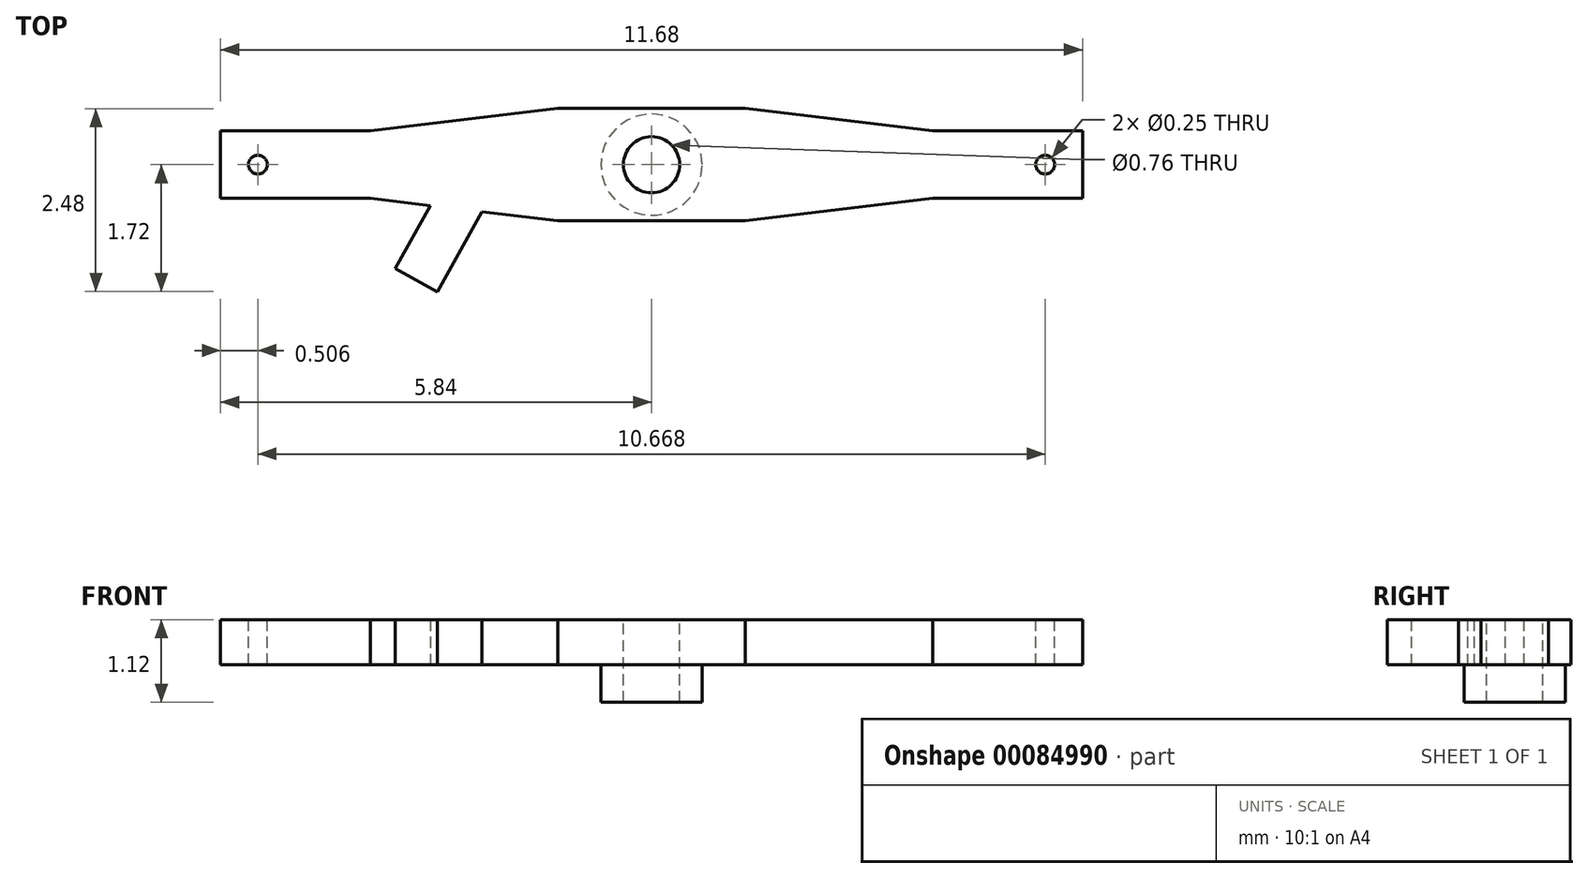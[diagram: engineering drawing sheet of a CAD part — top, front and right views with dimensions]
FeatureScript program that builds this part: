
annotation { "Feature Type Name" : "Feature", "Feature Type Description" : "" }
export const myFeature = defineFeature(function(context is Context, id is Id, definition is map)
    precondition{}
    {
        {
            var Q0;
            Q0=qCreatedBy(makeId("Top.planeOp"),FACE);
            var sketch = newSketch(context, id + "F0", { "sketchPlane" : qUnion([Q0])});
            skLineSegment(sketch, "E0.bottom", {"start": v(-1.27, 0.76) * mm, "end": v(1.27, 0.76) * mm});
            skLineSegment(sketch, "E0.top", {"start": v(-1.27, -0.76) * mm, "end": v(1.27, -0.76) * mm});
            skLineSegment(sketch, "E1.bottom", {"start": v(-5.84, 0.46) * mm, "end": v(-3.81, 0.46) * mm});
            skLineSegment(sketch, "E1.top", {"start": v(-5.84, -0.46) * mm, "end": v(-3.81, -0.46) * mm});
            skLineSegment(sketch, "E1.left", {"start": v(-5.84, 0.46) * mm, "end": v(-5.84, -0.46) * mm});
            skLineSegment(sketch, "E1.right", {"start": v(5.84, 0.46) * mm, "end": v(5.84, -0.46) * mm});
            skLineSegment(sketch, "E2", {"start": v(-1.27, 0.76) * mm, "end": v(-3.81, 0.46) * mm});
            skLineSegment(sketch, "E3", {"start": v(-3.81, -0.46) * mm, "end": v(-1.27, -0.76) * mm});
            skLineSegment(sketch, "E4", {"start": v(1.27, 0.76) * mm, "end": v(3.81, 0.46) * mm});
            skLineSegment(sketch, "E5", {"start": v(3.81, -0.46) * mm, "end": v(1.27, -0.76) * mm});
            skLineSegment(sketch, "E6.trimOffspring", {"start": v(3.81, 0.46) * mm, "end": v(5.84, 0.46) * mm});
            skLineSegment(sketch, "E7.trimOffspring", {"start": v(3.81, -0.46) * mm, "end": v(5.84, -0.46) * mm});
            skLineSegment(sketch, "E8", {"start": v(-3, -0.55) * mm, "end": v(-3.47, -1.4) * mm});
            skLineSegment(sketch, "E9", {"start": v(-3.47, -1.4) * mm, "end": v(-2.9, -1.72) * mm});
            skLineSegment(sketch, "E10", {"start": v(-2.9, -1.72) * mm, "end": v(-2.3, -0.64) * mm});
            skSolve(sketch);
        }
        {
            var Q0;
            Q0 = qSketchRegion(id + "F0", true);
            extrude(context, id + "F1", {"entities" : qUnion([Q0]), "depth" : 0.6 * mm});
        }
        {
            var Q0;
            Q0=makeQuery(id+"F1.opExtrude","CAP_FACE",FACE,{"disambiguationData":[OSD([sQuery(id+"F0.wireOp",EDGE,"E0.bottom"),sQuery(id+"F0.wireOp",EDGE,"E0.top"),sQuery(id+"F0.wireOp",EDGE,"E1.bottom"),sQuery(id+"F0.wireOp",EDGE,"E1.top"),sQuery(id+"F0.wireOp",EDGE,"E1.left"),sQuery(id+"F0.wireOp",EDGE,"E1.right"),sQuery(id+"F0.wireOp",EDGE,"E2"),sQuery(id+"F0.wireOp",EDGE,"E3"),sQuery(id+"F0.wireOp",EDGE,"E4"),sQuery(id+"F0.wireOp",EDGE,"E5"),sQuery(id+"F0.wireOp",EDGE,"E6.trimOffspring"),sQuery(id+"F0.wireOp",EDGE,"E7.trimOffspring")])],"isStart":false});
            var sketch = newSketch(context, id + "F2", { "sketchPlane" : qUnion([Q0])});
            skCircle(sketch, "E11", {"center": v(0, 0) * mm, "radius": 0.38 * mm});
            skSolve(sketch);
        }
        {
            var Q0;
            Q0 = qSketchRegion(id + "F2", true);
            extrude(context, id + "F3", {"entities" : qUnion([Q0]), "operationType" : NewBodyOperationType.REMOVE, "oppositeDirection" : true, "depth" : 25.4 * mm});
        }
        {
            var Q0;
            Q0=makeQuery(id+"F1.opExtrude","CAP_FACE",FACE,{"disambiguationData":[OSD([sQuery(id+"F0.wireOp",EDGE,"E0.bottom"),sQuery(id+"F0.wireOp",EDGE,"E0.top"),sQuery(id+"F0.wireOp",EDGE,"E1.bottom"),sQuery(id+"F0.wireOp",EDGE,"E1.top"),sQuery(id+"F0.wireOp",EDGE,"E1.left"),sQuery(id+"F0.wireOp",EDGE,"E1.right"),sQuery(id+"F0.wireOp",EDGE,"E2"),sQuery(id+"F0.wireOp",EDGE,"E3"),sQuery(id+"F0.wireOp",EDGE,"E4"),sQuery(id+"F0.wireOp",EDGE,"E5"),sQuery(id+"F0.wireOp",EDGE,"E6.trimOffspring"),sQuery(id+"F0.wireOp",EDGE,"E7.trimOffspring"),sQuery(id+"F0.wireOp",EDGE,"E8"),sQuery(id+"F0.wireOp",EDGE,"E9"),sQuery(id+"F0.wireOp",EDGE,"E10")])],"isStart":false});
            var sketch = newSketch(context, id + "F4", { "sketchPlane" : qUnion([Q0])});
            skCircle(sketch, "E12", {"center": v(-5.33, 0) * mm, "radius": 0.13 * mm});
            skCircle(sketch, "E13.MirrorC", {"center": v(5.33, 0) * mm, "radius": 0.13 * mm});
            skSolve(sketch);
        }
        {
            var Q0;
            Q0 = qSketchRegion(id + "F4", true);
            extrude(context, id + "F5", {"entities" : qUnion([Q0]), "operationType" : NewBodyOperationType.REMOVE, "oppositeDirection" : true, "depth" : 2.54 * mm});
        }
        {
            var Q0;
            Q0=qCreatedBy(makeId("Top.planeOp"),FACE);
            var sketch = newSketch(context, id + "F6", { "sketchPlane" : qUnion([Q0])});
            skCircle(sketch, "E14", {"center": v(0, 0) * mm, "radius": 0.38 * mm});
            skCircle(sketch, "E15", {"center": v(0, 0) * mm, "radius": 0.69 * mm});
            skSolve(sketch);
        }
        {
            var Q0;
            Q0 = qSketchRegion(id + "F6", true);
            extrude(context, id + "F7", {"entities" : qUnion([Q0]), "operationType" : NewBodyOperationType.ADD, "oppositeDirection" : true, "depth" : 0.5 * mm});
        }
    });
